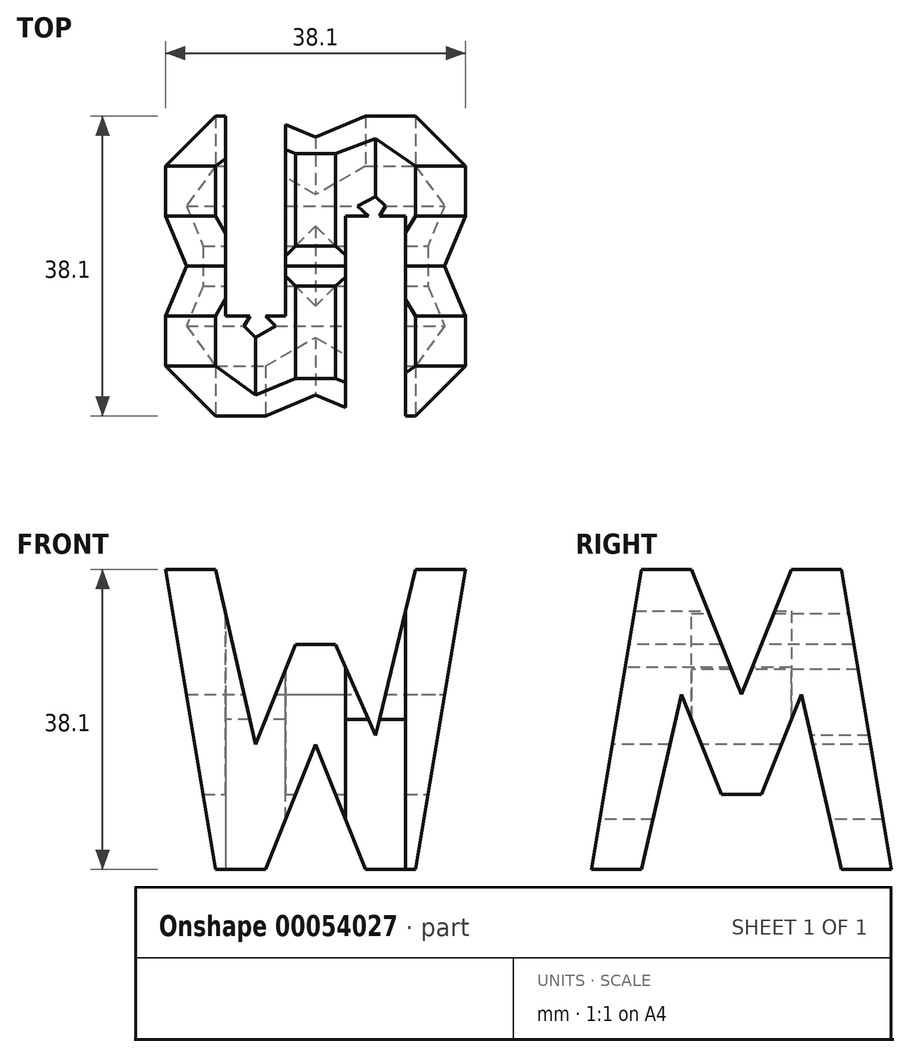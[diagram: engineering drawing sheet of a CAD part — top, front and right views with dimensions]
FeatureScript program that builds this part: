
annotation { "Feature Type Name" : "Feature", "Feature Type Description" : "" }
export const myFeature = defineFeature(function(context is Context, id is Id, definition is map)
    precondition{}
    {
        {
            var Q0;
            Q0=qCreatedBy(makeId("Right.planeOp"),FACE);
            var sketch = newSketch(context, id + "F0", { "sketchPlane" : qUnion([Q0])});
            skLineSegment(sketch, "E0.bottom", {"start": v(0, 0) * mm, "end": v(-38.1, 0) * mm});
            skLineSegment(sketch, "E0.top", {"start": v(0, 38.1) * mm, "end": v(-38.1, 38.1) * mm});
            skLineSegment(sketch, "E0.left", {"start": v(0, 0) * mm, "end": v(0, 38.1) * mm});
            skLineSegment(sketch, "E0.right", {"start": v(-38.1, 0) * mm, "end": v(-38.1, 38.1) * mm});
            skSolve(sketch);
        }
        {
            var Q0;
            Q0 = qSketchRegion(id + "F0", true);
            extrude(context, id + "F1", {"entities" : qUnion([Q0]), "depth" : 38.1 * mm});
        }
        {
            var Q0;
            Q0=qCreatedBy(makeId("Right.planeOp"),FACE);
            cPlane(context, id + "F2", {"entities" : qUnion([Q0]), "cplaneType" : CPlaneType.OFFSET, "offset" : 38.1 * mm, "width" : 152.4 * mm, "height" : 152.4 * mm});
        }
        {
            var Q0;
            Q0=qCreatedBy(makeId("Front.planeOp"),FACE);
            cPlane(context, id + "F3", {"entities" : qUnion([Q0]), "cplaneType" : CPlaneType.OFFSET, "offset" : 38.1 * mm, "width" : 152.4 * mm, "height" : 152.4 * mm});
        }
        {
            var Q0;
            Q0=qCreatedBy(makeId("Top.planeOp"),FACE);
            cPlane(context, id + "F4", {"entities" : qUnion([Q0]), "cplaneType" : CPlaneType.OFFSET, "offset" : 38.1 * mm, "width" : 152.4 * mm, "height" : 152.4 * mm});
        }
        {
            var Q0;
            Q0=qCreatedBy(id+"F3.planeOp",FACE);
            var sketch = newSketch(context, id + "F5", { "sketchPlane" : qUnion([Q0])});
            skLineSegment(sketch, "E1.bottom", {"start": v(0, 0) * mm, "end": v(38.1, 0) * mm});
            skLineSegment(sketch, "E1.top", {"start": v(0, 38.1) * mm, "end": v(38.1, 38.1) * mm});
            skLineSegment(sketch, "E1.left", {"start": v(0, 0) * mm, "end": v(0, 38.1) * mm});
            skLineSegment(sketch, "E1.right", {"start": v(38.1, 0) * mm, "end": v(38.1, 38.1) * mm});
            skLineSegment(sketch, "E2", {"start": v(0, 38.1) * mm, "end": v(6.35, 0) * mm});
            skLineSegment(sketch, "E3", {"start": v(6.35, 38.1) * mm, "end": v(11.43, 15.87) * mm});
            skLineSegment(sketch, "E4", {"start": v(11.43, 15.87) * mm, "end": v(16.51, 28.57) * mm});
            skLineSegment(sketch, "E5", {"start": v(16.51, 28.57) * mm, "end": v(21.59, 28.57) * mm});
            skLineSegment(sketch, "E6", {"start": v(21.59, 28.57) * mm, "end": v(26.67, 17.01) * mm});
            skLineSegment(sketch, "E7", {"start": v(26.67, 17.01) * mm, "end": v(31.75, 38.1) * mm});
            skLineSegment(sketch, "E8", {"start": v(12.7, 0) * mm, "end": v(19.05, 15.87) * mm});
            skLineSegment(sketch, "E9", {"start": v(19.05, 15.87) * mm, "end": v(25.4, 0) * mm});
            skLineSegment(sketch, "E10", {"start": v(38.1, 38.1) * mm, "end": v(31.75, 0) * mm});
            skSolve(sketch);
        }
        {
            var Q0;
            {var subQ0=sQuery(id+"F5.wireOp",EDGE,"E3");Q0=makeQuery(id+"F5.imprint","IMPRINT",FACE,{"disambiguationData":[TD([[makeQuery(id+"F5.imprint","IMPRINT",EDGE,{"derivedFrom":subQ0}),1.0]])]});}
            var Q1;
            {var subQ0=sQuery(id+"F5.wireOp",EDGE,"E1.left");Q1=makeQuery(id+"F5.imprint","IMPRINT",FACE,{"disambiguationData":[TD([[makeQuery(id+"F5.imprint","IMPRINT",EDGE,{"derivedFrom":subQ0}),-1.0]])]});}
            var Q2;
            {var subQ0=sQuery(id+"F5.wireOp",EDGE,"E1.right");Q2=makeQuery(id+"F5.imprint","IMPRINT",FACE,{"disambiguationData":[TD([[makeQuery(id+"F5.imprint","IMPRINT",EDGE,{"derivedFrom":subQ0}),1.0]])]});}
            var Q3;
            {var subQ0=sQuery(id+"F5.wireOp",EDGE,"E8");Q3=makeQuery(id+"F5.imprint","IMPRINT",FACE,{"disambiguationData":[TD([[makeQuery(id+"F5.imprint","IMPRINT",EDGE,{"derivedFrom":subQ0}),-1.0]])]});}
            extrude(context, id + "F6", {"entities" : qUnion([Q0, Q1, Q2, Q3]), "operationType" : NewBodyOperationType.REMOVE, "oppositeDirection" : true, "depth" : 38.1 * mm});
        }
        {
            var Q0;
            Q0=qCreatedBy(id+"F2.planeOp",FACE);
            var sketch = newSketch(context, id + "F7", { "sketchPlane" : qUnion([Q0])});
            skLineSegment(sketch, "E11.bottom", {"start": v(0, 0) * mm, "end": v(-38.1, 0) * mm});
            skLineSegment(sketch, "E11.top", {"start": v(0, 38.1) * mm, "end": v(-38.1, 38.1) * mm});
            skLineSegment(sketch, "E11.left", {"start": v(0, 0) * mm, "end": v(0, 38.1) * mm});
            skLineSegment(sketch, "E11.right", {"start": v(-38.1, 0) * mm, "end": v(-38.1, 38.1) * mm});
            skLineSegment(sketch, "E12", {"start": v(-38.1, 0) * mm, "end": v(-31.75, 38.1) * mm});
            skLineSegment(sketch, "E13", {"start": v(-6.35, 38.1) * mm, "end": v(0, 0) * mm});
            skLineSegment(sketch, "E14", {"start": v(-25.4, 38.1) * mm, "end": v(-19.05, 22.23) * mm});
            skLineSegment(sketch, "E15", {"start": v(-19.05, 22.23) * mm, "end": v(-12.7, 38.1) * mm});
            skLineSegment(sketch, "E16", {"start": v(-31.75, 0) * mm, "end": v(-26.67, 22.23) * mm});
            skLineSegment(sketch, "E17", {"start": v(-26.67, 22.23) * mm, "end": v(-21.59, 9.52) * mm});
            skLineSegment(sketch, "E18", {"start": v(-21.59, 9.52) * mm, "end": v(-16.5, 9.52) * mm});
            skLineSegment(sketch, "E19", {"start": v(-16.5, 9.52) * mm, "end": v(-11.43, 22.23) * mm});
            skLineSegment(sketch, "E20", {"start": v(-11.43, 22.23) * mm, "end": v(-6.35, 0) * mm});
            skSolve(sketch);
        }
        {
            var Q0;
            {var subQ0=sQuery(id+"F7.wireOp",EDGE,"E11.right");Q0=makeQuery(id+"F7.imprint","IMPRINT",FACE,{"disambiguationData":[TD([[makeQuery(id+"F7.imprint","IMPRINT",EDGE,{"derivedFrom":subQ0}),-1.0]])]});}
            var Q1;
            {var subQ0=sQuery(id+"F7.wireOp",EDGE,"E14");Q1=makeQuery(id+"F7.imprint","IMPRINT",FACE,{"disambiguationData":[TD([[makeQuery(id+"F7.imprint","IMPRINT",EDGE,{"derivedFrom":subQ0}),1.0]])]});}
            var Q2;
            {var subQ0=sQuery(id+"F7.wireOp",EDGE,"E16");Q2=makeQuery(id+"F7.imprint","IMPRINT",FACE,{"disambiguationData":[TD([[makeQuery(id+"F7.imprint","IMPRINT",EDGE,{"derivedFrom":subQ0}),-1.0]])]});}
            var Q3;
            {var subQ0=sQuery(id+"F7.wireOp",EDGE,"E11.left");Q3=makeQuery(id+"F7.imprint","IMPRINT",FACE,{"disambiguationData":[TD([[makeQuery(id+"F7.imprint","IMPRINT",EDGE,{"derivedFrom":subQ0}),1.0]])]});}
            extrude(context, id + "F8", {"entities" : qUnion([Q0, Q1, Q2, Q3]), "operationType" : NewBodyOperationType.REMOVE, "oppositeDirection" : true, "depth" : 38.1 * mm});
        }
        {
            var Q0;
            Q0=qCreatedBy(id+"F4.planeOp",FACE);
            var sketch = newSketch(context, id + "F9", { "sketchPlane" : qUnion([Q0])});
            skLineSegment(sketch, "E21.bottom", {"start": v(0, 0) * mm, "end": v(38.1, 0) * mm});
            skLineSegment(sketch, "E21.top", {"start": v(0, -38.1) * mm, "end": v(38.1, -38.1) * mm});
            skLineSegment(sketch, "E21.left", {"start": v(0, 0) * mm, "end": v(0, -38.1) * mm});
            skLineSegment(sketch, "E21.right", {"start": v(38.1, 0) * mm, "end": v(38.1, -38.1) * mm});
            skLineSegment(sketch, "E22", {"start": v(7.62, 0) * mm, "end": v(7.62, -25.4) * mm});
            skLineSegment(sketch, "E23", {"start": v(7.62, -25.4) * mm, "end": v(15.24, -25.4) * mm});
            skLineSegment(sketch, "E24", {"start": v(15.24, -25.4) * mm, "end": v(15.24, 0) * mm});
            skLineSegment(sketch, "E25", {"start": v(22.86, -38.1) * mm, "end": v(22.86, -12.7) * mm});
            skLineSegment(sketch, "E26", {"start": v(22.86, -12.7) * mm, "end": v(30.48, -12.7) * mm});
            skLineSegment(sketch, "E27", {"start": v(30.48, -12.7) * mm, "end": v(30.48, -38.1) * mm});
            skLineSegment(sketch, "E28", {"start": v(38.1, -38.1) * mm, "end": v(38.1, 0) * mm});
            skLineSegment(sketch, "E29", {"start": v(38.1, 0) * mm, "end": v(0, 0) * mm});
            skSolve(sketch);
        }
        {
            var Q0;
            {var subQ0=sQuery(id+"F9.wireOp",EDGE,"E22");Q0=makeQuery(id+"F9.imprint","IMPRINT",FACE,{"disambiguationData":[TD([[makeQuery(id+"F9.imprint","IMPRINT",EDGE,{"derivedFrom":subQ0}),1.0]])]});}
            var Q1;
            {var subQ0=sQuery(id+"F9.wireOp",EDGE,"E25");Q1=makeQuery(id+"F9.imprint","IMPRINT",FACE,{"disambiguationData":[TD([[makeQuery(id+"F9.imprint","IMPRINT",EDGE,{"derivedFrom":subQ0}),-1.0]])]});}
            extrude(context, id + "F10", {"entities" : qUnion([Q0, Q1]), "operationType" : NewBodyOperationType.REMOVE, "oppositeDirection" : true, "depth" : 38.1 * mm});
        }
    });
